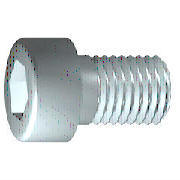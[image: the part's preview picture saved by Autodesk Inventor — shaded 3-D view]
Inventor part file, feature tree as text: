
AUTODESK INVENTOR PART (.ipt)
format: ipt  version: 2023.3 (Build 273359000, 359)  size: 186,368 bytes
history: native  units: mm (DEFAULTED — no unit token found)
features: sketch x2, other x1, extrude x1, plane x1, fillet x1
ambient origin geometry x7: Origin, YZ Plane, XY Plane, X Axis, Y Axis, Z Axis, Center Point
bodies: Solid1 (feature_tree)
feature tree (6):
  other  "Körper"
  extrude  "Loch"  Depth=4.0mm
  plane  "Work Plane1"
  fillet  "Fillet2"  Radius=4.0mm
  sketch  "Skizze1"  dims[d1=20.0mm d2=0.429515mm d3=4.0mm]
  sketch  "Skizze2"  dims[d4=2.0mm d5=60.0deg d6=4.0mm d7=4.0mm d8=3.464102mm d9=7.0mm d10=90.0deg d11=10.0mm d12=0.0mm d13=20.0mm d14=0.0mm d15=0.429415mm d16=0.429415mm d17=0.4mm d19=0.0mm d26=35.0mm d27=45.0deg d28=0.0mm d29=0.0mm d30=0.2mm]
